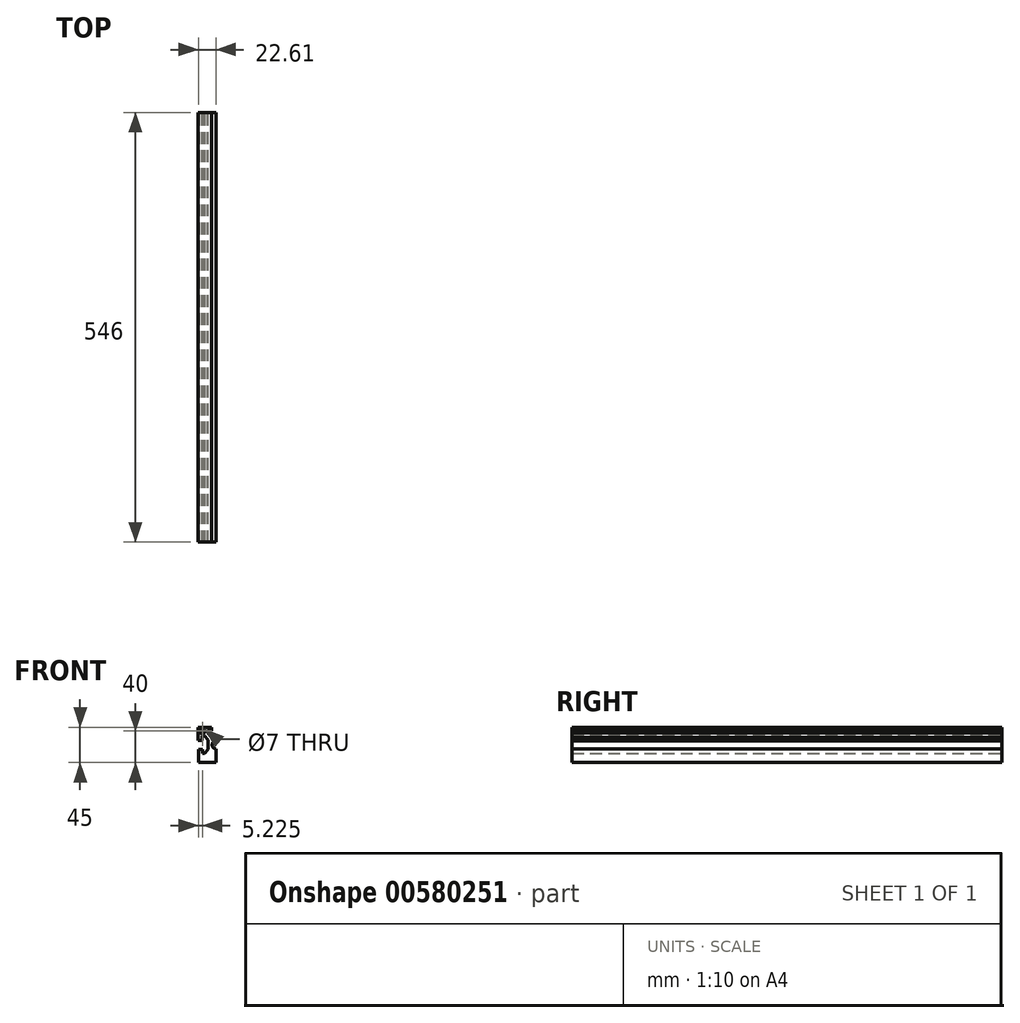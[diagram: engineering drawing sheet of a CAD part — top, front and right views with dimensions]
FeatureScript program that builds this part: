
annotation { "Feature Type Name" : "Feature", "Feature Type Description" : "" }
export const myFeature = defineFeature(function(context is Context, id is Id, definition is map)
    precondition{}
    {
        {
            var Q0;
            Q0=qCreatedBy(makeId("Front.planeOp"),FACE);
            var sketch = newSketch(context, id + "F0", { "sketchPlane" : qUnion([Q0])});
            skLineSegment(sketch, "E0", {"start": v(0, 0) * mm, "end": v(0, 32) * mm});
            skLineSegment(sketch, "E1", {"start": v(0, 0) * mm, "end": v(-22.5, 0) * mm});
            skLineSegment(sketch, "E2", {"start": v(-22.5, 0) * mm, "end": v(-22.5, 17) * mm});
            skLineSegment(sketch, "E3", {"start": v(-22.5, 17) * mm, "end": v(-17.5, 17) * mm});
            skLineSegment(sketch, "E4", {"start": v(-17.5, 17) * mm, "end": v(-17.5, 11.5) * mm});
            skLineSegment(sketch, "E5", {"start": v(-17.5, 11.5) * mm, "end": v(-14.5, 11.5) * mm});
            skLineSegment(sketch, "E6", {"start": v(0, 32) * mm, "end": v(-6, 32) * mm});
            skLineSegment(sketch, "E7", {"start": v(-5.61, 45) * mm, "end": v(-22.61, 45) * mm});
            skLineSegment(sketch, "E8", {"start": v(-5.61, 45) * mm, "end": v(-5.61, 40) * mm});
            skLineSegment(sketch, "E9", {"start": v(-11.11, 40) * mm, "end": v(-11.11, 37.5) * mm});
            skLineSegment(sketch, "E10", {"start": v(-5.61, 40) * mm, "end": v(-11.11, 40) * mm});
            skLineSegment(sketch, "E11", {"start": v(-11.11, 37.5) * mm, "end": v(-6, 32) * mm});
            skLineSegment(sketch, "E12", {"start": v(-22.61, 45) * mm, "end": v(-22.61, 28) * mm});
            skLineSegment(sketch, "E13", {"start": v(-22.61, 28) * mm, "end": v(-17.61, 28) * mm});
            skLineSegment(sketch, "E14", {"start": v(-17.61, 28) * mm, "end": v(-17.61, 34.06) * mm});
            skLineSegment(sketch, "E15", {"start": v(-17.61, 34.06) * mm, "end": v(-14.61, 34.06) * mm});
            skLineSegment(sketch, "E16", {"start": v(-10, 28.96) * mm, "end": v(-10, 16.96) * mm});
            skLineSegment(sketch, "E17", {"start": v(-14.61, 34.06) * mm, "end": v(-10, 28.96) * mm});
            skLineSegment(sketch, "E18", {"start": v(-14.5, 11.5) * mm, "end": v(-10, 16.96) * mm});
            skSolve(sketch);
        }
        {
            var Q0;
            Q0=makeQuery(id+"F0.imprint","IMPRINT",FACE,{"disambiguationData":[TD([[makeQuery(id+"F0.imprint","IMPRINT",EDGE,{"derivedFrom":sQuery(id+"F0.wireOp",EDGE,"E0")}),1.0]])]});
            var Q1;
            Q1=makeQuery(id+"F7SZdiq9qd4dseX_0.1.F0.imprint","IMPRINT",FACE,{"disambiguationData":[TD([[makeQuery(id+"F7SZdiq9qd4dseX_0.1.F0.imprint","IMPRINT",EDGE,{"derivedFrom":sQuery(id+"F7SZdiq9qd4dseX_0.1.F0.wireOp",EDGE,"E0")}),1.0]])]});
            var Q2;
            Q2=makeQuery(id+"F7SZdiq9qd4dseX_0.1.F0.imprint","IMPRINT",FACE,{"disambiguationData":[TD([[makeQuery(id+"F7SZdiq9qd4dseX_0.1.F0.imprint","IMPRINT",EDGE,{"derivedFrom":sQuery(id+"F7SZdiq9qd4dseX_0.1.F0.wireOp",EDGE,"E0")}),1.0]])]});
            var Q3;
            Q3=makeQuery(id+"FCfiFY75XbIrKH5_0.1.F0.imprint","IMPRINT",FACE,{"disambiguationData":[TD([[makeQuery(id+"FCfiFY75XbIrKH5_0.1.F0.imprint","IMPRINT",EDGE,{"derivedFrom":sQuery(id+"FCfiFY75XbIrKH5_0.1.F0.wireOp",EDGE,"E0")}),1.0]])]});
            var Q4;
            Q4=makeQuery(id+"FygOOUOEW6BidB4_0.1.FCfiFY75XbIrKH5_0.1.F0.imprint","IMPRINT",FACE,{"disambiguationData":[TD([[makeQuery(id+"FygOOUOEW6BidB4_0.1.FCfiFY75XbIrKH5_0.1.F0.imprint","IMPRINT",EDGE,{"derivedFrom":sQuery(id+"FygOOUOEW6BidB4_0.1.FCfiFY75XbIrKH5_0.1.F0.wireOp",EDGE,"E0")}),1.0]])]});
            extrude(context, id + "F1", {"entities" : qUnion([Q0, Q1, Q2, Q3, Q4]), "depth" : 546 * mm, "offsetDistance" : 25 * mm});
        }
        {
            var Q0;
            Q0=qCreatedBy(makeId("Front.planeOp"),FACE);
            var sketch = newSketch(context, id + "F2", { "sketchPlane" : qUnion([Q0])});
            skPoint(sketch, "E19", {"position": v(17.61, 40) * mm});
            skPoint(sketch, "E20", {"position": v(-17.39, 40) * mm});
            skPoint(sketch, "E21", {"position": v(-17.39, -40) * mm});
            skPoint(sketch, "E22", {"position": v(17.61, -40) * mm});
            skPoint(sketch, "E23", {"position": v(0, 22.5) * mm});
            skPoint(sketch, "E24", {"position": v(0, -22.5) * mm});
            skSolve(sketch);
        }
        {
            var Q0;
            Q0=sQuery(id+"F2.wireOp",VERTEX,"E19");
            var Q1;
            Q1=sQuery(id+"F2.wireOp",VERTEX,"E20");
            var Q2;
            Q2=sQuery(id+"F2.wireOp",VERTEX,"E21");
            var Q3;
            Q3=sQuery(id+"F2.wireOp",VERTEX,"E22");
            var Q4;
            Q4=makeQuery(id+"F1.opExtrude","SWEPT_BODY",BODY,{"disambiguationData":[OSD([sQuery(id+"F7SZdiq9qd4dseX_0.1.F0.wireOp",EDGE,"E0"),sQuery(id+"F7SZdiq9qd4dseX_0.1.F0.wireOp",EDGE,"E1"),sQuery(id+"F7SZdiq9qd4dseX_0.1.F0.wireOp",EDGE,"E2"),sQuery(id+"F7SZdiq9qd4dseX_0.1.F0.wireOp",EDGE,"E3"),sQuery(id+"F7SZdiq9qd4dseX_0.1.F0.wireOp",EDGE,"E4"),sQuery(id+"F7SZdiq9qd4dseX_0.1.F0.wireOp",EDGE,"E5"),sQuery(id+"F7SZdiq9qd4dseX_0.1.F0.wireOp",EDGE,"E6"),sQuery(id+"F7SZdiq9qd4dseX_0.1.F0.wireOp",EDGE,"E7"),sQuery(id+"F7SZdiq9qd4dseX_0.1.F0.wireOp",EDGE,"E8"),sQuery(id+"F7SZdiq9qd4dseX_0.1.F0.wireOp",EDGE,"E9"),sQuery(id+"F7SZdiq9qd4dseX_0.1.F0.wireOp",EDGE,"E10"),sQuery(id+"F7SZdiq9qd4dseX_0.1.F0.wireOp",EDGE,"E11"),sQuery(id+"F7SZdiq9qd4dseX_0.1.F0.wireOp",EDGE,"E12"),sQuery(id+"F7SZdiq9qd4dseX_0.1.F0.wireOp",EDGE,"E13"),sQuery(id+"F7SZdiq9qd4dseX_0.1.F0.wireOp",EDGE,"E14"),sQuery(id+"F7SZdiq9qd4dseX_0.1.F0.wireOp",EDGE,"E15"),sQuery(id+"F7SZdiq9qd4dseX_0.1.F0.wireOp",EDGE,"E16"),sQuery(id+"F7SZdiq9qd4dseX_0.1.F0.wireOp",EDGE,"E17"),sQuery(id+"F7SZdiq9qd4dseX_0.1.F0.wireOp",EDGE,"E18")])]});
            var Q5;
            Q5=makeQuery(id+"F1.opExtrude","SWEPT_BODY",BODY,{"disambiguationData":[OSD([sQuery(id+"F0.wireOp",EDGE,"E0"),sQuery(id+"F0.wireOp",EDGE,"E1"),sQuery(id+"F0.wireOp",EDGE,"E2"),sQuery(id+"F0.wireOp",EDGE,"E3"),sQuery(id+"F0.wireOp",EDGE,"E4"),sQuery(id+"F0.wireOp",EDGE,"E5"),sQuery(id+"F0.wireOp",EDGE,"E6"),sQuery(id+"F0.wireOp",EDGE,"E7"),sQuery(id+"F0.wireOp",EDGE,"E8"),sQuery(id+"F0.wireOp",EDGE,"E9"),sQuery(id+"F0.wireOp",EDGE,"E10"),sQuery(id+"F0.wireOp",EDGE,"E11"),sQuery(id+"F0.wireOp",EDGE,"E12"),sQuery(id+"F0.wireOp",EDGE,"E13"),sQuery(id+"F0.wireOp",EDGE,"E14"),sQuery(id+"F0.wireOp",EDGE,"E15"),sQuery(id+"F0.wireOp",EDGE,"E16"),sQuery(id+"F0.wireOp",EDGE,"E17"),sQuery(id+"F0.wireOp",EDGE,"E18")])]});
            var Q6;
            Q6=makeQuery(id+"F1.opExtrude","SWEPT_BODY",BODY,{"disambiguationData":[OSD([sQuery(id+"FCfiFY75XbIrKH5_0.1.F0.wireOp",EDGE,"E0"),sQuery(id+"FCfiFY75XbIrKH5_0.1.F0.wireOp",EDGE,"E1"),sQuery(id+"FCfiFY75XbIrKH5_0.1.F0.wireOp",EDGE,"E2"),sQuery(id+"FCfiFY75XbIrKH5_0.1.F0.wireOp",EDGE,"E3"),sQuery(id+"FCfiFY75XbIrKH5_0.1.F0.wireOp",EDGE,"E4"),sQuery(id+"FCfiFY75XbIrKH5_0.1.F0.wireOp",EDGE,"E5"),sQuery(id+"FCfiFY75XbIrKH5_0.1.F0.wireOp",EDGE,"E6"),sQuery(id+"FCfiFY75XbIrKH5_0.1.F0.wireOp",EDGE,"E7"),sQuery(id+"FCfiFY75XbIrKH5_0.1.F0.wireOp",EDGE,"E8"),sQuery(id+"FCfiFY75XbIrKH5_0.1.F0.wireOp",EDGE,"E9"),sQuery(id+"FCfiFY75XbIrKH5_0.1.F0.wireOp",EDGE,"E10"),sQuery(id+"FCfiFY75XbIrKH5_0.1.F0.wireOp",EDGE,"E11"),sQuery(id+"FCfiFY75XbIrKH5_0.1.F0.wireOp",EDGE,"E12"),sQuery(id+"FCfiFY75XbIrKH5_0.1.F0.wireOp",EDGE,"E13"),sQuery(id+"FCfiFY75XbIrKH5_0.1.F0.wireOp",EDGE,"E14"),sQuery(id+"FCfiFY75XbIrKH5_0.1.F0.wireOp",EDGE,"E15"),sQuery(id+"FCfiFY75XbIrKH5_0.1.F0.wireOp",EDGE,"E16"),sQuery(id+"FCfiFY75XbIrKH5_0.1.F0.wireOp",EDGE,"E17"),sQuery(id+"FCfiFY75XbIrKH5_0.1.F0.wireOp",EDGE,"E18")])]});
            var Q7;
            Q7=makeQuery(id+"F1.opExtrude","SWEPT_BODY",BODY,{"disambiguationData":[OSD([sQuery(id+"FygOOUOEW6BidB4_0.1.FCfiFY75XbIrKH5_0.1.F0.wireOp",EDGE,"E0"),sQuery(id+"FygOOUOEW6BidB4_0.1.FCfiFY75XbIrKH5_0.1.F0.wireOp",EDGE,"E1"),sQuery(id+"FygOOUOEW6BidB4_0.1.FCfiFY75XbIrKH5_0.1.F0.wireOp",EDGE,"E2"),sQuery(id+"FygOOUOEW6BidB4_0.1.FCfiFY75XbIrKH5_0.1.F0.wireOp",EDGE,"E3"),sQuery(id+"FygOOUOEW6BidB4_0.1.FCfiFY75XbIrKH5_0.1.F0.wireOp",EDGE,"E4"),sQuery(id+"FygOOUOEW6BidB4_0.1.FCfiFY75XbIrKH5_0.1.F0.wireOp",EDGE,"E5"),sQuery(id+"FygOOUOEW6BidB4_0.1.FCfiFY75XbIrKH5_0.1.F0.wireOp",EDGE,"E6"),sQuery(id+"FygOOUOEW6BidB4_0.1.FCfiFY75XbIrKH5_0.1.F0.wireOp",EDGE,"E7"),sQuery(id+"FygOOUOEW6BidB4_0.1.FCfiFY75XbIrKH5_0.1.F0.wireOp",EDGE,"E8"),sQuery(id+"FygOOUOEW6BidB4_0.1.FCfiFY75XbIrKH5_0.1.F0.wireOp",EDGE,"E9"),sQuery(id+"FygOOUOEW6BidB4_0.1.FCfiFY75XbIrKH5_0.1.F0.wireOp",EDGE,"E10"),sQuery(id+"FygOOUOEW6BidB4_0.1.FCfiFY75XbIrKH5_0.1.F0.wireOp",EDGE,"E11"),sQuery(id+"FygOOUOEW6BidB4_0.1.FCfiFY75XbIrKH5_0.1.F0.wireOp",EDGE,"E12"),sQuery(id+"FygOOUOEW6BidB4_0.1.FCfiFY75XbIrKH5_0.1.F0.wireOp",EDGE,"E13"),sQuery(id+"FygOOUOEW6BidB4_0.1.FCfiFY75XbIrKH5_0.1.F0.wireOp",EDGE,"E14"),sQuery(id+"FygOOUOEW6BidB4_0.1.FCfiFY75XbIrKH5_0.1.F0.wireOp",EDGE,"E15"),sQuery(id+"FygOOUOEW6BidB4_0.1.FCfiFY75XbIrKH5_0.1.F0.wireOp",EDGE,"E16"),sQuery(id+"FygOOUOEW6BidB4_0.1.FCfiFY75XbIrKH5_0.1.F0.wireOp",EDGE,"E17"),sQuery(id+"FygOOUOEW6BidB4_0.1.FCfiFY75XbIrKH5_0.1.F0.wireOp",EDGE,"E18")])]});
            hole(context, id + "F3", {"style" : HoleStyle.SIMPLE, "endStyle" : HoleEndStyle.THROUGH, "oppositeDirection" : true, "holeDiameter" : 7 * mm, "majorDiameter" : 12 * mm, "isTappedThrough" : true, "tappedDepth" : 8 * mm, "tapClearance" : 3, "startFromSketch" : true, "locations" : qUnion([Q0, Q1, Q2, Q3]), "scope" : qUnion([Q4, Q5, Q6, Q7])});
        }
        {
            var Q0;
            Q0=sQuery(id+"F2.wireOp",VERTEX,"E24");
            var Q1;
            Q1=sQuery(id+"F2.wireOp",VERTEX,"E23");
            var Q2;
            Q2=makeQuery(id+"F1.opExtrude","SWEPT_BODY",BODY,{"disambiguationData":[OSD([sQuery(id+"F0.wireOp",EDGE,"E0"),sQuery(id+"F0.wireOp",EDGE,"E1"),sQuery(id+"F0.wireOp",EDGE,"E2"),sQuery(id+"F0.wireOp",EDGE,"E3"),sQuery(id+"F0.wireOp",EDGE,"E4"),sQuery(id+"F0.wireOp",EDGE,"E5"),sQuery(id+"F0.wireOp",EDGE,"E6"),sQuery(id+"F0.wireOp",EDGE,"E7"),sQuery(id+"F0.wireOp",EDGE,"E8"),sQuery(id+"F0.wireOp",EDGE,"E9"),sQuery(id+"F0.wireOp",EDGE,"E10"),sQuery(id+"F0.wireOp",EDGE,"E11"),sQuery(id+"F0.wireOp",EDGE,"E12"),sQuery(id+"F0.wireOp",EDGE,"E13"),sQuery(id+"F0.wireOp",EDGE,"E14"),sQuery(id+"F0.wireOp",EDGE,"E15"),sQuery(id+"F0.wireOp",EDGE,"E16"),sQuery(id+"F0.wireOp",EDGE,"E17"),sQuery(id+"F0.wireOp",EDGE,"E18")])]});
            var Q3;
            Q3=makeQuery(id+"F1.opExtrude","SWEPT_BODY",BODY,{"disambiguationData":[OSD([sQuery(id+"F7SZdiq9qd4dseX_0.1.F0.wireOp",EDGE,"E0"),sQuery(id+"F7SZdiq9qd4dseX_0.1.F0.wireOp",EDGE,"E1"),sQuery(id+"F7SZdiq9qd4dseX_0.1.F0.wireOp",EDGE,"E2"),sQuery(id+"F7SZdiq9qd4dseX_0.1.F0.wireOp",EDGE,"E3"),sQuery(id+"F7SZdiq9qd4dseX_0.1.F0.wireOp",EDGE,"E4"),sQuery(id+"F7SZdiq9qd4dseX_0.1.F0.wireOp",EDGE,"E5"),sQuery(id+"F7SZdiq9qd4dseX_0.1.F0.wireOp",EDGE,"E6"),sQuery(id+"F7SZdiq9qd4dseX_0.1.F0.wireOp",EDGE,"E7"),sQuery(id+"F7SZdiq9qd4dseX_0.1.F0.wireOp",EDGE,"E8"),sQuery(id+"F7SZdiq9qd4dseX_0.1.F0.wireOp",EDGE,"E9"),sQuery(id+"F7SZdiq9qd4dseX_0.1.F0.wireOp",EDGE,"E10"),sQuery(id+"F7SZdiq9qd4dseX_0.1.F0.wireOp",EDGE,"E11"),sQuery(id+"F7SZdiq9qd4dseX_0.1.F0.wireOp",EDGE,"E12"),sQuery(id+"F7SZdiq9qd4dseX_0.1.F0.wireOp",EDGE,"E13"),sQuery(id+"F7SZdiq9qd4dseX_0.1.F0.wireOp",EDGE,"E14"),sQuery(id+"F7SZdiq9qd4dseX_0.1.F0.wireOp",EDGE,"E15"),sQuery(id+"F7SZdiq9qd4dseX_0.1.F0.wireOp",EDGE,"E16"),sQuery(id+"F7SZdiq9qd4dseX_0.1.F0.wireOp",EDGE,"E17"),sQuery(id+"F7SZdiq9qd4dseX_0.1.F0.wireOp",EDGE,"E18")])]});
            var Q4;
            Q4=makeQuery(id+"F1.opExtrude","SWEPT_BODY",BODY,{"disambiguationData":[OSD([sQuery(id+"FCfiFY75XbIrKH5_0.1.F0.wireOp",EDGE,"E0"),sQuery(id+"FCfiFY75XbIrKH5_0.1.F0.wireOp",EDGE,"E1"),sQuery(id+"FCfiFY75XbIrKH5_0.1.F0.wireOp",EDGE,"E2"),sQuery(id+"FCfiFY75XbIrKH5_0.1.F0.wireOp",EDGE,"E3"),sQuery(id+"FCfiFY75XbIrKH5_0.1.F0.wireOp",EDGE,"E4"),sQuery(id+"FCfiFY75XbIrKH5_0.1.F0.wireOp",EDGE,"E5"),sQuery(id+"FCfiFY75XbIrKH5_0.1.F0.wireOp",EDGE,"E6"),sQuery(id+"FCfiFY75XbIrKH5_0.1.F0.wireOp",EDGE,"E7"),sQuery(id+"FCfiFY75XbIrKH5_0.1.F0.wireOp",EDGE,"E8"),sQuery(id+"FCfiFY75XbIrKH5_0.1.F0.wireOp",EDGE,"E9"),sQuery(id+"FCfiFY75XbIrKH5_0.1.F0.wireOp",EDGE,"E10"),sQuery(id+"FCfiFY75XbIrKH5_0.1.F0.wireOp",EDGE,"E11"),sQuery(id+"FCfiFY75XbIrKH5_0.1.F0.wireOp",EDGE,"E12"),sQuery(id+"FCfiFY75XbIrKH5_0.1.F0.wireOp",EDGE,"E13"),sQuery(id+"FCfiFY75XbIrKH5_0.1.F0.wireOp",EDGE,"E14"),sQuery(id+"FCfiFY75XbIrKH5_0.1.F0.wireOp",EDGE,"E15"),sQuery(id+"FCfiFY75XbIrKH5_0.1.F0.wireOp",EDGE,"E16"),sQuery(id+"FCfiFY75XbIrKH5_0.1.F0.wireOp",EDGE,"E17"),sQuery(id+"FCfiFY75XbIrKH5_0.1.F0.wireOp",EDGE,"E18")])]});
            var Q5;
            Q5=makeQuery(id+"F1.opExtrude","SWEPT_BODY",BODY,{"disambiguationData":[OSD([sQuery(id+"FygOOUOEW6BidB4_0.1.FCfiFY75XbIrKH5_0.1.F0.wireOp",EDGE,"E0"),sQuery(id+"FygOOUOEW6BidB4_0.1.FCfiFY75XbIrKH5_0.1.F0.wireOp",EDGE,"E1"),sQuery(id+"FygOOUOEW6BidB4_0.1.FCfiFY75XbIrKH5_0.1.F0.wireOp",EDGE,"E2"),sQuery(id+"FygOOUOEW6BidB4_0.1.FCfiFY75XbIrKH5_0.1.F0.wireOp",EDGE,"E3"),sQuery(id+"FygOOUOEW6BidB4_0.1.FCfiFY75XbIrKH5_0.1.F0.wireOp",EDGE,"E4"),sQuery(id+"FygOOUOEW6BidB4_0.1.FCfiFY75XbIrKH5_0.1.F0.wireOp",EDGE,"E5"),sQuery(id+"FygOOUOEW6BidB4_0.1.FCfiFY75XbIrKH5_0.1.F0.wireOp",EDGE,"E6"),sQuery(id+"FygOOUOEW6BidB4_0.1.FCfiFY75XbIrKH5_0.1.F0.wireOp",EDGE,"E7"),sQuery(id+"FygOOUOEW6BidB4_0.1.FCfiFY75XbIrKH5_0.1.F0.wireOp",EDGE,"E8"),sQuery(id+"FygOOUOEW6BidB4_0.1.FCfiFY75XbIrKH5_0.1.F0.wireOp",EDGE,"E9"),sQuery(id+"FygOOUOEW6BidB4_0.1.FCfiFY75XbIrKH5_0.1.F0.wireOp",EDGE,"E10"),sQuery(id+"FygOOUOEW6BidB4_0.1.FCfiFY75XbIrKH5_0.1.F0.wireOp",EDGE,"E11"),sQuery(id+"FygOOUOEW6BidB4_0.1.FCfiFY75XbIrKH5_0.1.F0.wireOp",EDGE,"E12"),sQuery(id+"FygOOUOEW6BidB4_0.1.FCfiFY75XbIrKH5_0.1.F0.wireOp",EDGE,"E13"),sQuery(id+"FygOOUOEW6BidB4_0.1.FCfiFY75XbIrKH5_0.1.F0.wireOp",EDGE,"E14"),sQuery(id+"FygOOUOEW6BidB4_0.1.FCfiFY75XbIrKH5_0.1.F0.wireOp",EDGE,"E15"),sQuery(id+"FygOOUOEW6BidB4_0.1.FCfiFY75XbIrKH5_0.1.F0.wireOp",EDGE,"E16"),sQuery(id+"FygOOUOEW6BidB4_0.1.FCfiFY75XbIrKH5_0.1.F0.wireOp",EDGE,"E17"),sQuery(id+"FygOOUOEW6BidB4_0.1.FCfiFY75XbIrKH5_0.1.F0.wireOp",EDGE,"E18")])]});
            hole(context, id + "F4", {"style" : HoleStyle.SIMPLE, "endStyle" : HoleEndStyle.THROUGH, "oppositeDirection" : true, "standardTappedOrClearance" : lookupTablePath({ "standard" : "ISO", "engagement" : "75%", "pitch" : "1.75 mm", "size" : "M12", "type" : "Tapped" }), "standardBlindInLast" : lookupTablePath({ "standard" : "ISO", "engagement" : "75%", "pitch" : "1.75 mm", "size" : "M12", "type" : "Tapped" }), "holeDiameter" : 10.3 * mm, "majorDiameter" : 12 * mm, "showTappedDepth" : true, "isTappedThrough" : true, "tappedDepth" : 8 * mm, "tapClearance" : 3, "startFromSketch" : true, "locations" : qUnion([Q0, Q1]), "scope" : qUnion([Q2, Q3, Q4, Q5])});
        }
    });
